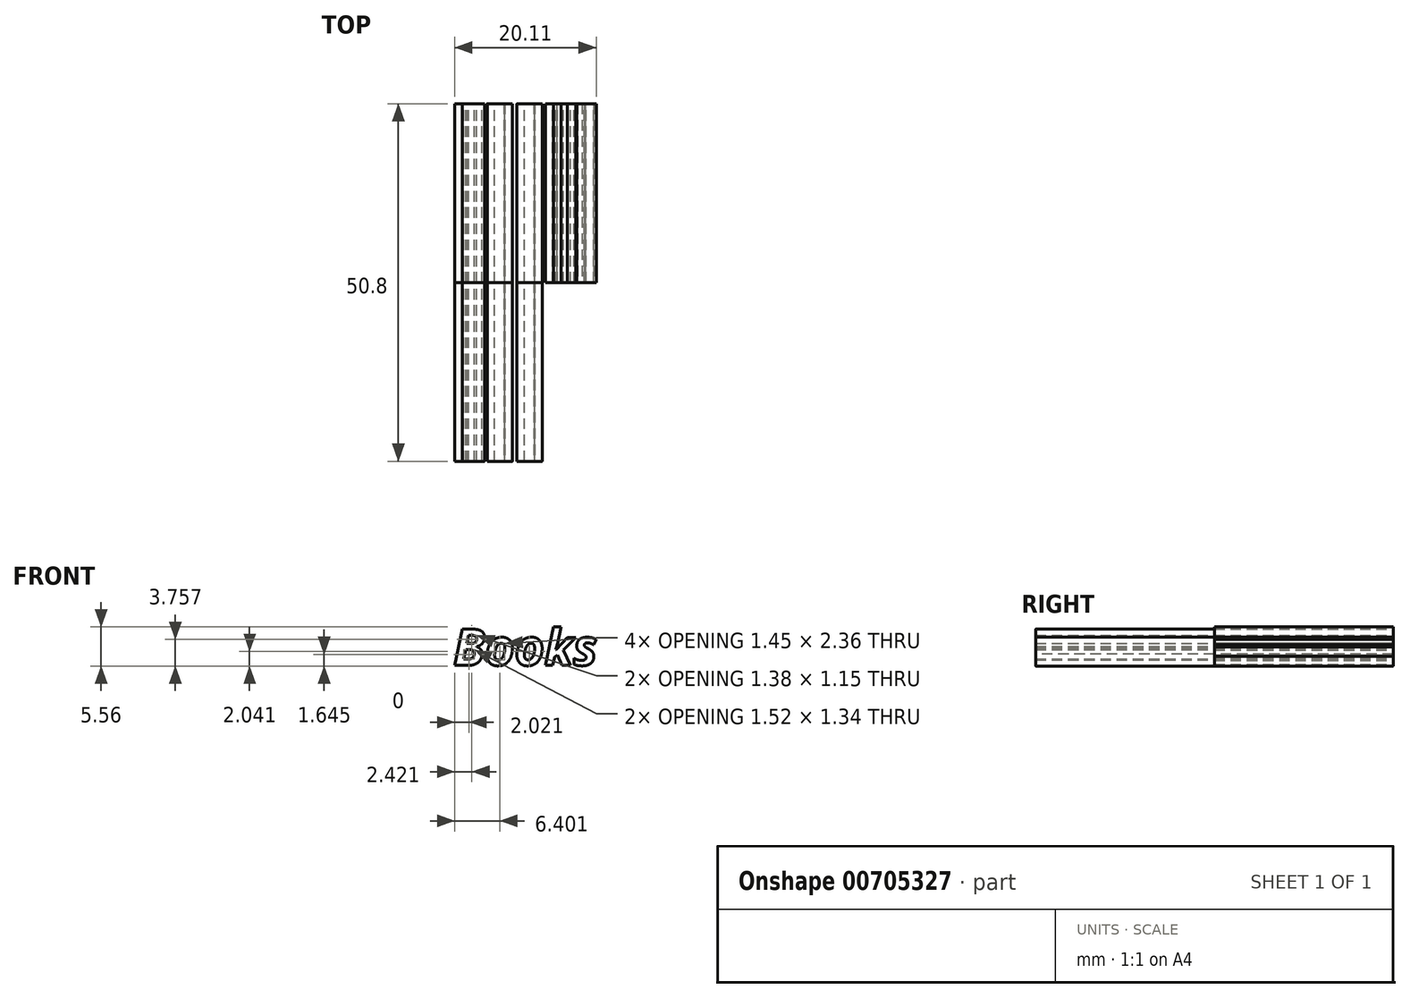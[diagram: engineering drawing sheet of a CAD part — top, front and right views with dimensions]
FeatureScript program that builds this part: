
annotation { "Feature Type Name" : "Feature", "Feature Type Description" : "" }
export const myFeature = defineFeature(function(context is Context, id is Id, definition is map)
    precondition{}
    {
        {
            var Q0;
            Q0=qCreatedBy(makeId("Front.planeOp"),FACE);
            var sketch = newSketch(context, id + "F0", { "sketchPlane" : qUnion([Q0])});
            skText(sketch, "E0", { "text": "Books", "fontName": "OpenSans-BoldItalic.ttf"});
            const initialGuessF0  = {"E0": [-0.0542, 0.0481, 1, 0, 0.0052]};
            skSetInitialGuess(sketch, initialGuessF0);
            skSolve(sketch);
        }
        {
            var Q0;
            Q0 = qSketchRegion(id + "F0", true);
            extrude(context, id + "F1", {"entities" : qUnion([Q0]), "depth" : 25.4 * mm, "offsetDistance" : 25.4 * mm});
        }
        {
            var Q0;
            Q0=makeQuery(id+"F1.opExtrude","CAP_FACE",FACE,{"disambiguationData":[OSD([sQuery(id+"F0.wireOp",EDGE,"E0.sketch_text.stroke-24"),sQuery(id+"F0.wireOp",EDGE,"E0.sketch_text.stroke-25"),sQuery(id+"F0.wireOp",EDGE,"E0.sketch_text.stroke-26"),sQuery(id+"F0.wireOp",EDGE,"E0.sketch_text.stroke-27"),sQuery(id+"F0.wireOp",EDGE,"E0.sketch_text.stroke-28"),sQuery(id+"F0.wireOp",EDGE,"E0.sketch_text.stroke-29"),sQuery(id+"F0.wireOp",EDGE,"E0.sketch_text.stroke-30"),sQuery(id+"F0.wireOp",EDGE,"E0.sketch_text.stroke-31"),sQuery(id+"F0.wireOp",EDGE,"E0.sketch_text.stroke-32"),sQuery(id+"F0.wireOp",EDGE,"E0.sketch_text.stroke-33"),sQuery(id+"F0.wireOp",EDGE,"E0.sketch_text.stroke-34"),sQuery(id+"F0.wireOp",EDGE,"E0.sketch_text.stroke-35"),sQuery(id+"F0.wireOp",EDGE,"E0.sketch_text.stroke-36"),sQuery(id+"F0.wireOp",EDGE,"E0.sketch_text.stroke-37"),sQuery(id+"F0.wireOp",EDGE,"E0.sketch_text.stroke-38"),sQuery(id+"F0.wireOp",EDGE,"E0.sketch_text.stroke-39"),sQuery(id+"F0.wireOp",EDGE,"E0.sketch_text.stroke-40"),sQuery(id+"F0.wireOp",EDGE,"E0.sketch_text.stroke-41")])],"isStart":false});
            var Q1;
            Q1=makeQuery(id+"F1.opExtrude","CAP_FACE",FACE,{"disambiguationData":[OSD([sQuery(id+"F0.wireOp",EDGE,"E0.sketch_text.stroke-0"),sQuery(id+"F0.wireOp",EDGE,"E0.sketch_text.stroke-1"),sQuery(id+"F0.wireOp",EDGE,"E0.sketch_text.stroke-2"),sQuery(id+"F0.wireOp",EDGE,"E0.sketch_text.stroke-3"),sQuery(id+"F0.wireOp",EDGE,"E0.sketch_text.stroke-4"),sQuery(id+"F0.wireOp",EDGE,"E0.sketch_text.stroke-5"),sQuery(id+"F0.wireOp",EDGE,"E0.sketch_text.stroke-6"),sQuery(id+"F0.wireOp",EDGE,"E0.sketch_text.stroke-7"),sQuery(id+"F0.wireOp",EDGE,"E0.sketch_text.stroke-8"),sQuery(id+"F0.wireOp",EDGE,"E0.sketch_text.stroke-9"),sQuery(id+"F0.wireOp",EDGE,"E0.sketch_text.stroke-10"),sQuery(id+"F0.wireOp",EDGE,"E0.sketch_text.stroke-11"),sQuery(id+"F0.wireOp",EDGE,"E0.sketch_text.stroke-12"),sQuery(id+"F0.wireOp",EDGE,"E0.sketch_text.stroke-13"),sQuery(id+"F0.wireOp",EDGE,"E0.sketch_text.stroke-14"),sQuery(id+"F0.wireOp",EDGE,"E0.sketch_text.stroke-15"),sQuery(id+"F0.wireOp",EDGE,"E0.sketch_text.stroke-16"),sQuery(id+"F0.wireOp",EDGE,"E0.sketch_text.stroke-17"),sQuery(id+"F0.wireOp",EDGE,"E0.sketch_text.stroke-18"),sQuery(id+"F0.wireOp",EDGE,"E0.sketch_text.stroke-19"),sQuery(id+"F0.wireOp",EDGE,"E0.sketch_text.stroke-20"),sQuery(id+"F0.wireOp",EDGE,"E0.sketch_text.stroke-21"),sQuery(id+"F0.wireOp",EDGE,"E0.sketch_text.stroke-22"),sQuery(id+"F0.wireOp",EDGE,"E0.sketch_text.stroke-23")])],"isStart":false});
            var Q2;
            Q2=makeQuery(id+"F1.opExtrude","CAP_FACE",FACE,{"disambiguationData":[OSD([sQuery(id+"F0.wireOp",EDGE,"E0.sketch_text.stroke-42"),sQuery(id+"F0.wireOp",EDGE,"E0.sketch_text.stroke-43"),sQuery(id+"F0.wireOp",EDGE,"E0.sketch_text.stroke-44"),sQuery(id+"F0.wireOp",EDGE,"E0.sketch_text.stroke-45"),sQuery(id+"F0.wireOp",EDGE,"E0.sketch_text.stroke-46"),sQuery(id+"F0.wireOp",EDGE,"E0.sketch_text.stroke-47"),sQuery(id+"F0.wireOp",EDGE,"E0.sketch_text.stroke-48"),sQuery(id+"F0.wireOp",EDGE,"E0.sketch_text.stroke-49"),sQuery(id+"F0.wireOp",EDGE,"E0.sketch_text.stroke-50"),sQuery(id+"F0.wireOp",EDGE,"E0.sketch_text.stroke-51"),sQuery(id+"F0.wireOp",EDGE,"E0.sketch_text.stroke-52"),sQuery(id+"F0.wireOp",EDGE,"E0.sketch_text.stroke-53"),sQuery(id+"F0.wireOp",EDGE,"E0.sketch_text.stroke-54"),sQuery(id+"F0.wireOp",EDGE,"E0.sketch_text.stroke-55"),sQuery(id+"F0.wireOp",EDGE,"E0.sketch_text.stroke-56"),sQuery(id+"F0.wireOp",EDGE,"E0.sketch_text.stroke-57"),sQuery(id+"F0.wireOp",EDGE,"E0.sketch_text.stroke-58"),sQuery(id+"F0.wireOp",EDGE,"E0.sketch_text.stroke-59")])],"isStart":false});
            extrude(context, id + "F2", {"entities" : qUnion([Q0, Q1, Q2]), "depth" : 25.4 * mm, "offsetDistance" : 25.4 * mm});
        }
    });
